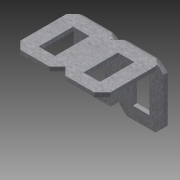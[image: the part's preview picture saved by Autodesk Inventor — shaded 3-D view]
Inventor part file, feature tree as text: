
AUTODESK INVENTOR PART (.ipt)
format: ipt  version: 2012 (Build 160160000, 160)  size: 1,704,448 bytes
history: native  units: in
note: dims shown in document units (in); Inventor stores cm internally (conversion verified against a paired STEP export)
features: sketch x2, other x1, imported_body x1, plane x1, split x1
ambient origin geometry x8: Origin, YZ Plane, XZ Plane, XY Plane, X Axis, Y Axis, Z Axis, Center Point
feature tree (6):
  parser-record x1  (decoder bookkeeping rows leaked as tree rows — omitted from the tree; the rows remain in map.json)
  imported_body  "Base1"
  sketch  "Sketch1"  dims[d0=13.7795in d2=0.5in d3=0.3937in d5=1.0in]
  sketch  "Sketch2"  dims[d7=13.7795in d9=0.5in d10=0.3937in d12=1.0in d14=-1.0in]
  plane  "Work Plane1"
  split  "Split1"
